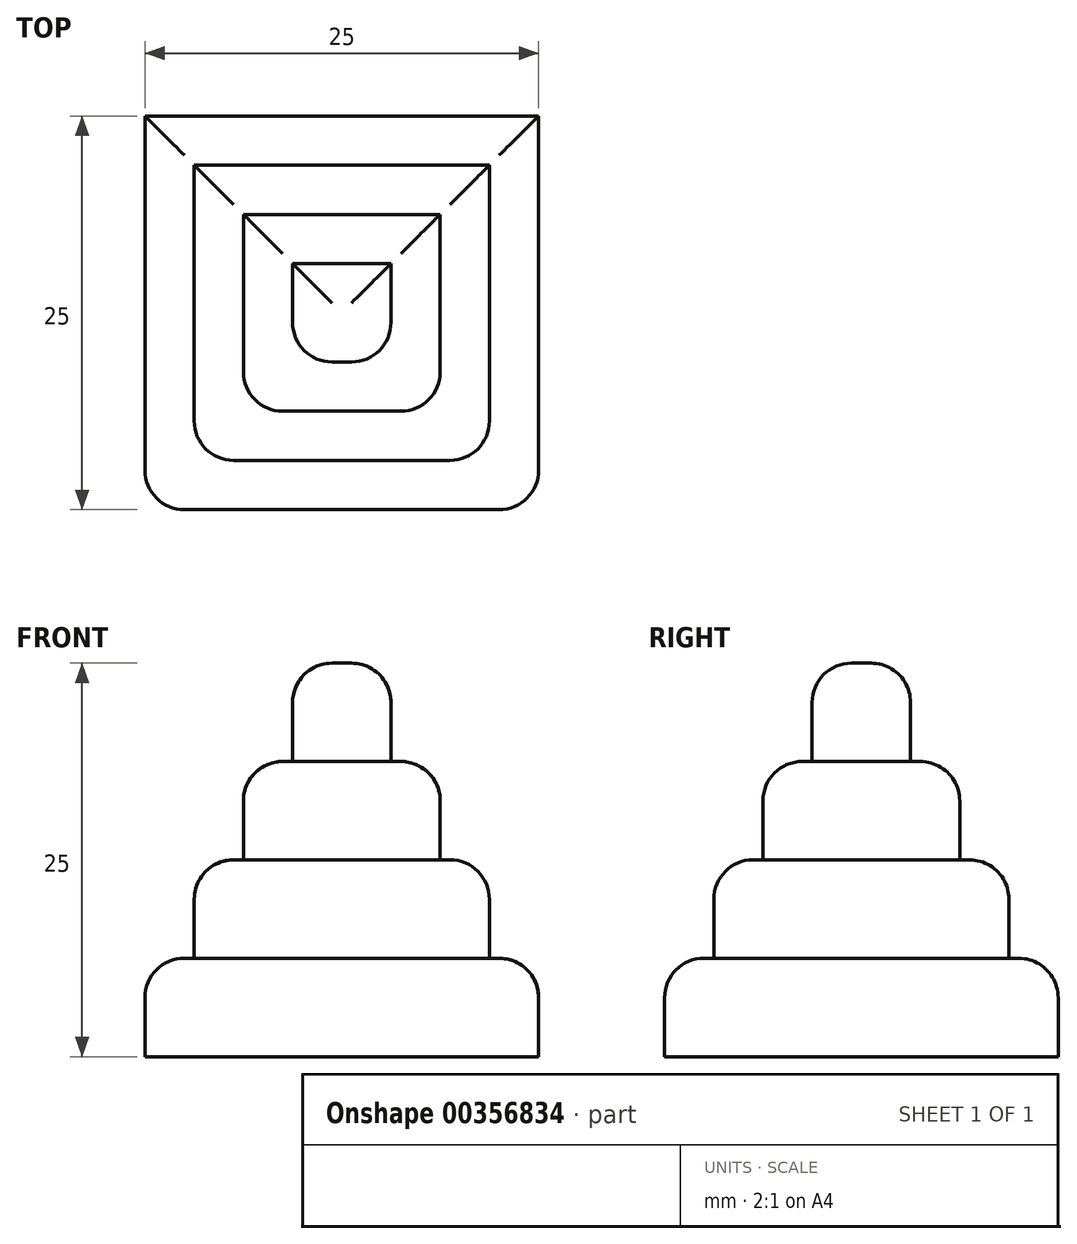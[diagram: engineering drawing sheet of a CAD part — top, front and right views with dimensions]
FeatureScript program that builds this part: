
annotation { "Feature Type Name" : "Feature", "Feature Type Description" : "" }
export const myFeature = defineFeature(function(context is Context, id is Id, definition is map)
    precondition{}
    {
        {
            assignVariable(context, id + "F0", {"name" : "Size", "anyValue" : 25});
        }
        {
            var Q0;
            Q0=qCreatedBy(makeId("Top.planeOp"),FACE);
            var sketch = newSketch(context, id + "F1", { "sketchPlane" : qUnion([Q0])});
            skLineSegment(sketch, "E0.bottom", {"start": v(0, 0) * mm, "end": v(25, 0) * mm});
            skLineSegment(sketch, "E0.top", {"start": v(0, 25) * mm, "end": v(25, 25) * mm});
            skLineSegment(sketch, "E0.left", {"start": v(0, 0) * mm, "end": v(0, 25) * mm});
            skLineSegment(sketch, "E0.right", {"start": v(25, 0) * mm, "end": v(25, 25) * mm});
            skLineSegment(sketch, "E1.0", {"start": v(3.12, 21.88) * mm, "end": v(21.87, 21.88) * mm});
            skLineSegment(sketch, "E1.1", {"start": v(3.12, 3.12) * mm, "end": v(3.12, 21.88) * mm});
            skLineSegment(sketch, "E1.2", {"start": v(3.12, 3.12) * mm, "end": v(21.88, 3.12) * mm});
            skLineSegment(sketch, "E1.3", {"start": v(21.88, 3.12) * mm, "end": v(21.87, 21.88) * mm});
            skLineSegment(sketch, "E2.0", {"start": v(6.25, 18.75) * mm, "end": v(18.75, 18.75) * mm});
            skLineSegment(sketch, "E2.1", {"start": v(6.25, 6.25) * mm, "end": v(6.25, 18.75) * mm});
            skLineSegment(sketch, "E2.2", {"start": v(6.25, 6.25) * mm, "end": v(18.75, 6.25) * mm});
            skLineSegment(sketch, "E2.3", {"start": v(18.75, 6.25) * mm, "end": v(18.75, 18.75) * mm});
            skLineSegment(sketch, "E3.0", {"start": v(9.37, 15.63) * mm, "end": v(15.62, 15.63) * mm});
            skLineSegment(sketch, "E3.1", {"start": v(9.37, 9.37) * mm, "end": v(9.37, 15.63) * mm});
            skLineSegment(sketch, "E3.2", {"start": v(9.37, 9.37) * mm, "end": v(15.62, 9.37) * mm});
            skLineSegment(sketch, "E3.3", {"start": v(15.62, 9.37) * mm, "end": v(15.62, 15.63) * mm});
            skSolve(sketch);
        }
        {
            var Q0;
            Q0=makeQuery(id+"F1.imprint","IMPRINT",FACE,{"disambiguationData":[TD([[makeQuery(id+"F1.imprint","IMPRINT",EDGE,{"derivedFrom":sQuery(id+"F1.wireOp",EDGE,"E0.bottom")}),1.0]])]});
            extrude(context, id + "F2", {"entities" : qUnion([Q0]), "depth" : (getVariable(context, 'Size') * 0.25) * mm});
        }
        {
            var Q0;
            Q0=makeQuery(id+"F1.imprint","IMPRINT",FACE,{"disambiguationData":[TD([[makeQuery(id+"F1.imprint","IMPRINT",EDGE,{"derivedFrom":sQuery(id+"F1.wireOp",EDGE,"E1.0")}),-1.0]])]});
            extrude(context, id + "F3", {"entities" : qUnion([Q0]), "operationType" : NewBodyOperationType.ADD, "depth" : (getVariable(context, 'Size') * 0.5) * mm});
        }
        {
            var Q0;
            Q0=makeQuery(id+"F1.imprint","IMPRINT",FACE,{"disambiguationData":[TD([[makeQuery(id+"F1.imprint","IMPRINT",EDGE,{"derivedFrom":sQuery(id+"F1.wireOp",EDGE,"E2.0")}),-1.0]])]});
            extrude(context, id + "F4", {"entities" : qUnion([Q0]), "operationType" : NewBodyOperationType.ADD, "depth" : (getVariable(context, 'Size') * 0.75) * mm});
        }
        {
            var Q0;
            Q0=makeQuery(id+"F1.imprint","IMPRINT",FACE,{"disambiguationData":[TD([[makeQuery(id+"F1.imprint","IMPRINT",EDGE,{"derivedFrom":sQuery(id+"F1.wireOp",EDGE,"E3.0")}),-1.0]])]});
            extrude(context, id + "F5", {"entities" : qUnion([Q0]), "operationType" : NewBodyOperationType.ADD, "depth" : (getVariable(context, 'Size')) * mm});
        }
        {
            var Q0;
            Q0=makeQuery(id+"F4.opExtrude","CAP_EDGE",EDGE,{"disambiguationData":[OSD([sQuery(id+"F1.wireOp",EDGE,"E2.3")])],"isStart":false});
            var Q1;
            Q1=makeQuery(id+"F4.opExtrude","CAP_EDGE",EDGE,{"disambiguationData":[OSD([sQuery(id+"F1.wireOp",EDGE,"E2.0")])],"isStart":false});
            var Q2;
            Q2=makeQuery(id+"F4.opExtrude","CAP_EDGE",EDGE,{"disambiguationData":[OSD([sQuery(id+"F1.wireOp",EDGE,"E2.1")])],"isStart":false});
            var Q3;
            Q3=makeQuery(id+"F4.opExtrude","CAP_EDGE",EDGE,{"disambiguationData":[OSD([sQuery(id+"F1.wireOp",EDGE,"E2.2")])],"isStart":false});
            var Q4;
            Q4=makeQuery(id+"F5.opExtrude","CAP_FACE",FACE,{"disambiguationData":[OSD([sQuery(id+"F1.wireOp",EDGE,"E3.0"),sQuery(id+"F1.wireOp",EDGE,"E3.1"),sQuery(id+"F1.wireOp",EDGE,"E3.2"),sQuery(id+"F1.wireOp",EDGE,"E3.3")])],"isStart":false});
            var Q5;
            Q5=makeQuery(id+"F3.opExtrude","CAP_EDGE",EDGE,{"disambiguationData":[OSD([sQuery(id+"F1.wireOp",EDGE,"E1.2")])],"isStart":false});
            var Q6;
            Q6=makeQuery(id+"F3.opExtrude","CAP_EDGE",EDGE,{"disambiguationData":[OSD([sQuery(id+"F1.wireOp",EDGE,"E1.3")])],"isStart":false});
            var Q7;
            Q7=makeQuery(id+"F3.opExtrude","CAP_EDGE",EDGE,{"disambiguationData":[OSD([sQuery(id+"F1.wireOp",EDGE,"E1.0")])],"isStart":false});
            var Q8;
            Q8=makeQuery(id+"F3.opExtrude","CAP_EDGE",EDGE,{"disambiguationData":[OSD([sQuery(id+"F1.wireOp",EDGE,"E1.1")])],"isStart":false});
            var Q9;
            Q9=makeQuery(id+"F2.opExtrude","CAP_EDGE",EDGE,{"disambiguationData":[OSD([sQuery(id+"F1.wireOp",EDGE,"E0.top")])],"isStart":false});
            var Q10;
            Q10=makeQuery(id+"F2.opExtrude","CAP_EDGE",EDGE,{"disambiguationData":[OSD([sQuery(id+"F1.wireOp",EDGE,"E0.left")])],"isStart":false});
            var Q11;
            Q11=makeQuery(id+"F2.opExtrude","CAP_EDGE",EDGE,{"disambiguationData":[OSD([sQuery(id+"F1.wireOp",EDGE,"E0.bottom")])],"isStart":false});
            var Q12;
            Q12=makeQuery(id+"F5.opExtrude","SWEPT_EDGE",EDGE,{"disambiguationData":[OSD([sQuery(id+"F1.wireOp",EDGE,"E3.2"),sQuery(id+"F1.wireOp",EDGE,"E3.3")])]});
            var Q13;
            Q13=makeQuery(id+"F5.opExtrude","SWEPT_EDGE",EDGE,{"disambiguationData":[OSD([sQuery(id+"F1.wireOp",EDGE,"E3.1"),sQuery(id+"F1.wireOp",EDGE,"E3.2")])]});
            var Q14;
            Q14=makeQuery(id+"F4.opExtrude","SWEPT_EDGE",EDGE,{"disambiguationData":[OSD([sQuery(id+"F1.wireOp",EDGE,"E2.1"),sQuery(id+"F1.wireOp",EDGE,"E2.2")])]});
            var Q15;
            Q15=makeQuery(id+"F4.opExtrude","SWEPT_EDGE",EDGE,{"disambiguationData":[OSD([sQuery(id+"F1.wireOp",EDGE,"E2.2"),sQuery(id+"F1.wireOp",EDGE,"E2.3")])]});
            var Q16;
            Q16=makeQuery(id+"F3.opExtrude","SWEPT_EDGE",EDGE,{"disambiguationData":[OSD([sQuery(id+"F1.wireOp",EDGE,"E1.1"),sQuery(id+"F1.wireOp",EDGE,"E1.2")])]});
            var Q17;
            Q17=makeQuery(id+"F3.opExtrude","SWEPT_EDGE",EDGE,{"disambiguationData":[OSD([sQuery(id+"F1.wireOp",EDGE,"E1.2"),sQuery(id+"F1.wireOp",EDGE,"E1.3")])]});
            var Q18;
            Q18=makeQuery(id+"F2.opExtrude","CAP_EDGE",EDGE,{"disambiguationData":[OSD([sQuery(id+"F1.wireOp",EDGE,"E0.right")])],"isStart":false});
            var Q19;
            Q19=makeQuery(id+"F2.opExtrude","SWEPT_EDGE",EDGE,{"disambiguationData":[OSD([sQuery(id+"F1.wireOp",EDGE,"E0.bottom"),sQuery(id+"F1.wireOp",EDGE,"E0.right")])]});
            var Q20;
            Q20=makeQuery(id+"F2.opExtrude","SWEPT_EDGE",EDGE,{"disambiguationData":[OSD([sQuery(id+"F1.wireOp",EDGE,"E0.bottom"),sQuery(id+"F1.wireOp",EDGE,"E0.left")])]});
            fillet(context, id + "F6", {"entities" : qUnion([Q0, Q1, Q2, Q3, Q4, Q5, Q6, Q7, Q8, Q9, Q10, Q11, Q12, Q13, Q14, Q15, Q16, Q17, Q18, Q19, Q20]), "radius" : (getVariable(context, 'Size') / 10) * mm, "tangentPropagation" : true, "allowEdgeOverflow" : false});
        }
    });
